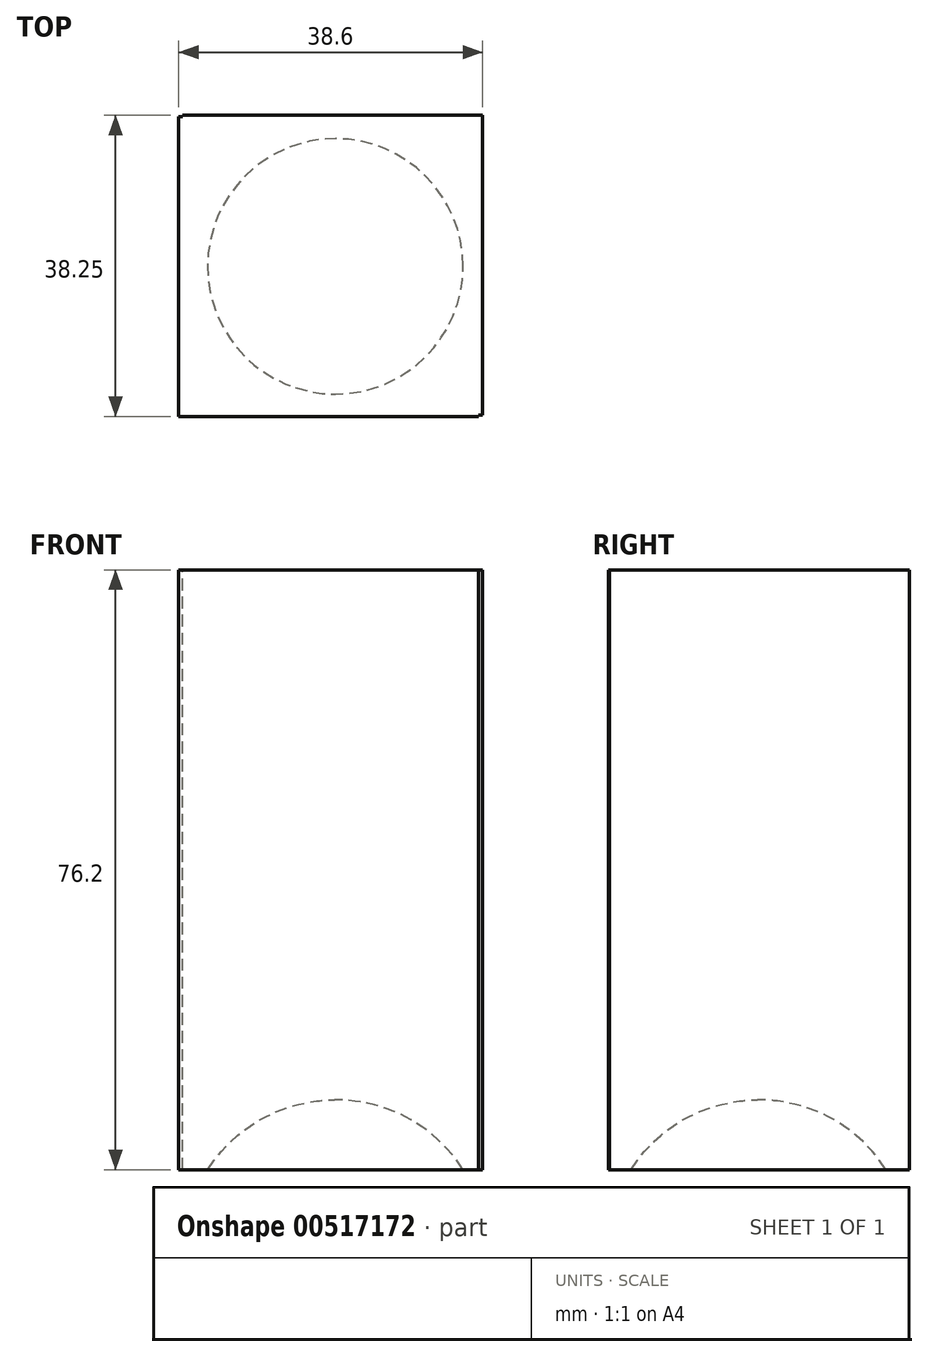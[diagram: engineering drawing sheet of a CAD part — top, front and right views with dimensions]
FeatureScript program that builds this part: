
annotation { "Feature Type Name" : "Feature", "Feature Type Description" : "" }
export const myFeature = defineFeature(function(context is Context, id is Id, definition is map)
    precondition{}
    {
        {
            var Q0;
            Q0=qCreatedBy(makeId("Front.planeOp"),FACE);
            var sketch = newSketch(context, id + "F0", { "sketchPlane" : qUnion([Q0])});
            skLineSegment(sketch, "E0", {"start": v(-38.41, 8.85) * mm, "end": v(-38.41, -29.25) * mm});
            skArc(sketch, "E1", {"start": v(-38.41, -29.25) * mm, "mid": v(-19.23, -10.2) * mm, "end": v(-38.41, 8.85) * mm});
            skSolve(sketch);
        }
        {
            var Q0;
            Q0=makeQuery(id+"F0.imprint","IMPRINT",FACE,{"disambiguationData":[TD([[makeQuery(id+"F0.imprint","IMPRINT",EDGE,{"derivedFrom":sQuery(id+"F0.wireOp",EDGE,"E0")}),1.0]])]});
            var Q1;
            Q1=sQuery(id+"F0.wireOp",EDGE,"E0");
            revolve(context, id + "F1", {"entities" : qUnion([Q0]), "axis" : qUnion([Q1]), "revolveType" : RevolveType.FULL});
        }
        {
            var Q0;
            Q0=qCreatedBy(makeId("Top.planeOp"),FACE);
            var sketch = newSketch(context, id + "F2", { "sketchPlane" : qUnion([Q0])});
            skLineSegment(sketch, "E2.bottom", {"start": v(-58.32, -19.05) * mm, "end": v(-20.22, -19.05) * mm});
            skLineSegment(sketch, "E2.top", {"start": v(-58.32, 19.05) * mm, "end": v(-20.22, 19.05) * mm});
            skLineSegment(sketch, "E2.left", {"start": v(-58.32, -19.05) * mm, "end": v(-58.32, 19.05) * mm});
            skLineSegment(sketch, "E2.right", {"start": v(-20.22, -19.05) * mm, "end": v(-20.22, 19.05) * mm});
            skPoint(sketch, "E2.middle", {"position": v(-39.27, 0) * mm});
            skSolve(sketch);
        }
        {
            var Q0;
            Q0=makeQuery(id+"F2.imprint","IMPRINT",FACE,{"disambiguationData":[TD([[makeQuery(id+"F2.imprint","IMPRINT",EDGE,{"derivedFrom":sQuery(id+"F2.wireOp",EDGE,"E2.bottom")}),1.0]])]});
            extrude(context, id + "F3", {"entities" : qUnion([Q0]), "operationType" : NewBodyOperationType.ADD, "depth" : 38.1 * mm, "offsetDistance" : 25.4 * mm});
        }
        {
            var Q0;
            Q0=qCreatedBy(makeId("Top.planeOp"),FACE);
            var sketch = newSketch(context, id + "F4", { "sketchPlane" : qUnion([Q0])});
            skLineSegment(sketch, "E3.bottom", {"start": v(-57.82, -18.9) * mm, "end": v(-19.72, -18.9) * mm});
            skLineSegment(sketch, "E3.top", {"start": v(-57.82, 19.2) * mm, "end": v(-19.72, 19.2) * mm});
            skLineSegment(sketch, "E3.left", {"start": v(-57.82, -18.9) * mm, "end": v(-57.82, 19.2) * mm});
            skLineSegment(sketch, "E3.right", {"start": v(-19.72, -18.9) * mm, "end": v(-19.72, 19.2) * mm});
            skSolve(sketch);
        }
        {
            var Q0;
            Q0=makeQuery(id+"F4.imprint","IMPRINT",FACE,{"disambiguationData":[TD([[makeQuery(id+"F4.imprint","IMPRINT",EDGE,{"derivedFrom":sQuery(id+"F4.wireOp",EDGE,"E3.bottom")}),1.0]])]});
            extrude(context, id + "F5", {"entities" : qUnion([Q0]), "operationType" : NewBodyOperationType.ADD, "depth" : 38.1 * mm, "offsetDistance" : 25.4 * mm});
        }
        {
            var Q0;
            Q0=makeQuery(id+"F5.boolean.opBoolean","MERGE",FACE,{"derivedFrom":[makeQuery(id+"F3.opExtrude","CAP_FACE",FACE,{"disambiguationData":[OSD([sQuery(id+"F2.wireOp",EDGE,"E2.bottom"),sQuery(id+"F2.wireOp",EDGE,"E2.top"),sQuery(id+"F2.wireOp",EDGE,"E2.left"),sQuery(id+"F2.wireOp",EDGE,"E2.right")])],"isStart":false}),makeQuery(id+"F5.opExtrude","CAP_FACE",FACE,{"disambiguationData":[OSD([sQuery(id+"F4.wireOp",EDGE,"E3.bottom"),sQuery(id+"F4.wireOp",EDGE,"E3.top"),sQuery(id+"F4.wireOp",EDGE,"E3.left"),sQuery(id+"F4.wireOp",EDGE,"E3.right")])],"isStart":false})]});
            extrude(context, id + "F6", {"entities" : qUnion([Q0]), "operationType" : NewBodyOperationType.ADD, "depth" : 38.1 * mm, "offsetDistance" : 25.4 * mm});
        }
    });
